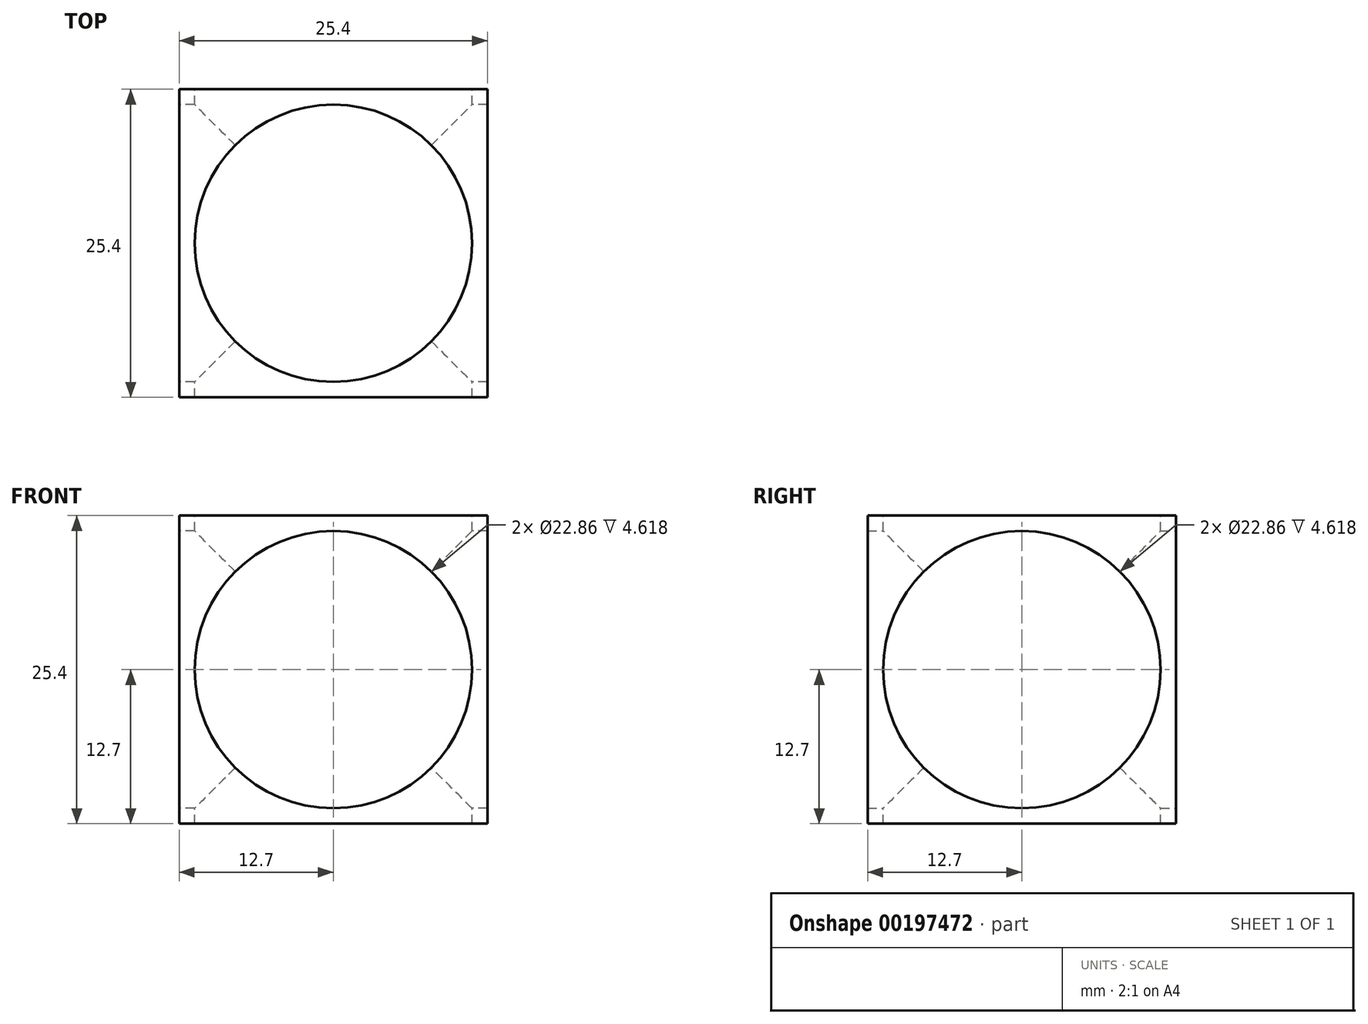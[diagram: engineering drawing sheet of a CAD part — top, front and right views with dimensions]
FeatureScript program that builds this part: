
annotation { "Feature Type Name" : "Feature", "Feature Type Description" : "" }
export const myFeature = defineFeature(function(context is Context, id is Id, definition is map)
    precondition{}
    {
        {
            var Q0;
            Q0=qCreatedBy(makeId("Top.planeOp"),FACE);
            var sketch = newSketch(context, id + "F0", { "sketchPlane" : qUnion([Q0])});
            skPoint(sketch, "E0.0", {"position": v(0, 0) * mm});
            skLineSegment(sketch, "E1.bottom", {"start": v(0, 0) * mm, "end": v(25.4, 0) * mm});
            skLineSegment(sketch, "E1.top", {"start": v(0, 25.4) * mm, "end": v(25.4, 25.4) * mm});
            skLineSegment(sketch, "E1.left", {"start": v(0, 0) * mm, "end": v(0, 25.4) * mm});
            skLineSegment(sketch, "E1.right", {"start": v(25.4, 0) * mm, "end": v(25.4, 25.4) * mm});
            skSolve(sketch);
        }
        {
            var Q0;
            Q0 = qSketchRegion(id + "F0", true);
            extrude(context, id + "F1", {"entities" : qUnion([Q0]), "depth" : 25.4 * mm});
        }
        {
            var Q0;
            Q0=makeQuery(id+"F1.opExtrude","CAP_FACE",FACE,{"disambiguationData":[OSD([sQuery(id+"F0.wireOp",EDGE,"E1.bottom"),sQuery(id+"F0.wireOp",EDGE,"E1.top"),sQuery(id+"F0.wireOp",EDGE,"E1.left"),sQuery(id+"F0.wireOp",EDGE,"E1.right")])],"isStart":false});
            var sketch = newSketch(context, id + "F2", { "sketchPlane" : qUnion([Q0])});
            skCircle(sketch, "E2", {"center": v(12.7, 12.7) * mm, "radius": 11.43 * mm});
            skPoint(sketch, "E2.centerSnap0", {"position": v(25.4, 12.7) * mm});
            skPoint(sketch, "E2.centerSnap1", {"position": v(12.7, 0) * mm});
            skSolve(sketch);
        }
        {
            var Q0;
            Q0 = qSketchRegion(id + "F2", true);
            extrude(context, id + "F3", {"entities" : qUnion([Q0]), "operationType" : NewBodyOperationType.REMOVE, "endBound" : BoundingType.THROUGH_ALL, "oppositeDirection" : true, "depth" : 25.4 * mm});
        }
        {
            var Q0;
            Q0=makeQuery(id+"F1.opExtrude","SWEPT_FACE",FACE,{"disambiguationData":[OSD([sQuery(id+"F0.wireOp",EDGE,"E1.left")])]});
            var sketch = newSketch(context, id + "F4", { "sketchPlane" : qUnion([Q0])});
            skCircle(sketch, "E3", {"center": v(-12.7, 12.7) * mm, "radius": 11.43 * mm});
            skPoint(sketch, "E3.centerSnap0", {"position": v(-12.7, 25.4) * mm});
            skPoint(sketch, "E3.centerSnap1", {"position": v(-25.4, 12.7) * mm});
            skSolve(sketch);
        }
        {
            var Q0;
            Q0 = qSketchRegion(id + "F4", true);
            extrude(context, id + "F5", {"entities" : qUnion([Q0]), "operationType" : NewBodyOperationType.REMOVE, "endBound" : BoundingType.THROUGH_ALL, "oppositeDirection" : true, "depth" : 25.4 * mm});
        }
        {
            var Q0;
            Q0=makeQuery(id+"F1.opExtrude","SWEPT_FACE",FACE,{"disambiguationData":[OSD([sQuery(id+"F0.wireOp",EDGE,"E1.top")])]});
            var sketch = newSketch(context, id + "F6", { "sketchPlane" : qUnion([Q0])});
            skCircle(sketch, "E4", {"center": v(-12.7, 12.7) * mm, "radius": 11.43 * mm});
            skPoint(sketch, "E4.centerSnap0", {"position": v(-12.7, 0) * mm});
            skPoint(sketch, "E4.centerSnap1", {"position": v(0, 12.7) * mm});
            skSolve(sketch);
        }
        {
            var Q0;
            Q0 = qSketchRegion(id + "F6", true);
            extrude(context, id + "F7", {"entities" : qUnion([Q0]), "operationType" : NewBodyOperationType.REMOVE, "endBound" : BoundingType.THROUGH_ALL, "oppositeDirection" : true, "depth" : 25.4 * mm});
        }
    });
